# Revit family: ITK_Шина заземления_Непосредственная установка
name_source: partatom
category: Обобщенные модели
units: mm (PartAtom-declared; Revit-internal decimal feet)

## family parameters
Всегда вертикально = Да
Может служить основой для арматурных стержней = Нет
На основе рабочей плоскости = Нет
Общий = Нет
При загрузке вырезать с полостями = Нет
Размер круглого соединителя = Использовать диаметр
Тип детали = Нормальный
Точка расчета площади = Нет

## types (2) — shared parameters
ADSK_URL страницы изделия = https://www.itk-group.ru
ADSK_Версия Revit = 2019
ADSK_Версия семейства = 1.0
ADSK_Группирование = I. ЩИТЫ И ПУЛЬТЫ
ADSK_Завод-изготовитель = IEK
ADSK_Материал наименование = Медь
IEK_URL = https://www.itk-group.ru
KSI_CMa_Строительные материалы = 10.2.01.03
KSI_CPr_Строительные изделия = 20.5.03.03
URL = https://www.iek.ru
Изготовитель = ITK
Тип монтажа = Непосредственная установка

## per-type parameters (varying)
| type | ADSK_Единица измерения | ADSK_Код изделия | ADSK_Масса | ADSK_Наименование | IEK_Описание | IEK_Цена за единицу |
| В1990хШ1000хГ10хЧерная | компл | ZP-SP05-42U-A-1000 | 22 | ITK by ZPAS Панель боковая 2 секции 42U тип A 1000 черная | Удобный доступ к оборудованию благодаря боковым панелям, состоящим из 2 секций. Доступны в двух вариантах, отличающихся глубиной. Боковые панели типа A (мелкие): - позволяют открывать дверь под углом до 270 градусов; - увеличивают общую ширину шкафа на 3 мм с каждой стороны. Боковые панели типа B (глубокие): - обеспечивают необходимое монтажное пространство в шкафах шириной 600 мм для установки блоков розеток между боковой панелью и вертикальным монтажным профилем; - увеличивают общую ширину шкафа на 11 мм с каждой стороны. | 21219.08 |
| ER-12 | шт | ER-12-325-M1 | 0.58 | ITK Шина заземления 483х25x3мм медь ШМТ М1 12 точек подключения. М6 | Совместимы со всеми 19" шкафами и стойками ITK.
Удобны в монтаже и эксплуатации.
Устанавливается на вертикальные монтажные профили.
Материал медь марки М1.
Соответствие российским и международным стандартам.
Все шины идут с крепежом.
Поставляются в качественной упаковке. | 1017 |
